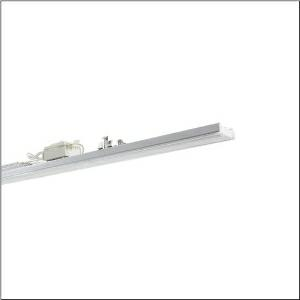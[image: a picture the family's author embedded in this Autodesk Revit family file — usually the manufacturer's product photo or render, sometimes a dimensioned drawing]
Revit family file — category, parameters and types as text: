
# Revit family: licross_r__11_recessed_ho_51tl1edn4d5s_5c77
name_source: partatom
category: Lighting Fixtures
units: mm (PartAtom-declared; Revit-internal decimal feet)

## family parameters
Cut with Voids When Loaded = No
Host = Face
Light Source = No
Part Type = Normal
Room Calculation Point = No
Round Connector Dimension = Use Diameter
Shared = No

## types (1)
- --- (1 x LED, 13670 lm, 76.8 W, 4000K)
    Apparent Load = 77 VA
    CIE Flux Codes = 85 95 99 100 100
    Color Rendering = 80
    Color Temperature = 4000K
    Default Elevation = 1800 mm
    Description = Licross® 11 Recessed HO, luminaire insert, of sheet steel, coil coated, white, length: 1.500mm, width: 66mm, height: 67mm, LED rated luminous flux: 13.670lm, light colour: 840, control gear: DALI 2, with plug, 5-pole, with phase selection, mains connection: 220..240V, AC, 50/60Hz, rated input power: 77W, halogen-free wiring, primary light control with lens, of plastic, primary optical cover: cover, of PMMA, light emission: direct distribution, primary light characteristic: symmetric, protection rating (complete): IP40, insulation class (complete): insulation class I (protective earthing), certification: CE, ENEC, VDE, UKCA, protection symbol: D if used in an environment without relevant dust loads with corresponding accessories, impact resistance: IK06, permissible ambient temperature for indoor applications: -25..+30°C, corresponds to IFS (International Featured Standards) requirements for safety and quality in the food industry, reducing of maximum allowable ambient temperature of 5°C with ceiling mounting, LABS conformity tested according to VDMA 24364:2018-05, packaging unit: 1 piece
    Height = 58 mm
    Lamp = 1 x LED
    Lamp Light Flux = 13670 lm
    Lamp Power = 76.8 W
    Lamp count = 1
    Length = 1500 mm
    Luminous efficacy = 178 lm/W
    Manufacturer = Siteco
    ModVariant = No
    Model = 51TL1EDN4D5S
    Mounting Place = Ceiling
    Mounting Type = Pendant
    Number of Poles = 1
    OnlyDefault = Yes
    Power Factor = 1
    Product Name = Licross® 11 Recessed HO
    Product group = luminaire insert
    ProductGroupID = 902
    Protection Class = Protection class I
    Protection Degree = IP 40
    RLX_Detail_Level = 1
    RLX_Emergency_Light_Flux = 0 lm
    RLX_Emergency_Type = 0
    RLX_Emergency_Type_DB = No
    RlxData = <blob elided: 24725 chars, md5=ba664dd8>
    Socket = socket
    Standby Power = 0 W
    System Light Flux = 13670 lm
    System Power = 77 W
    Type Comments = factory setting: luminous flux: 100 % | dim-lin: 254 | 522 mA
    Type Image = l_1296930.jpg
    URL = http://relux.com
    VarID = @adj_095924
    Voltage = 0 V
    Weight = 0.00 kg
    Width = 66 mm

## geometry (parser evidence)
native form markers: Blend x4, Sweep x10
no freeform markers — native parametric forms only
